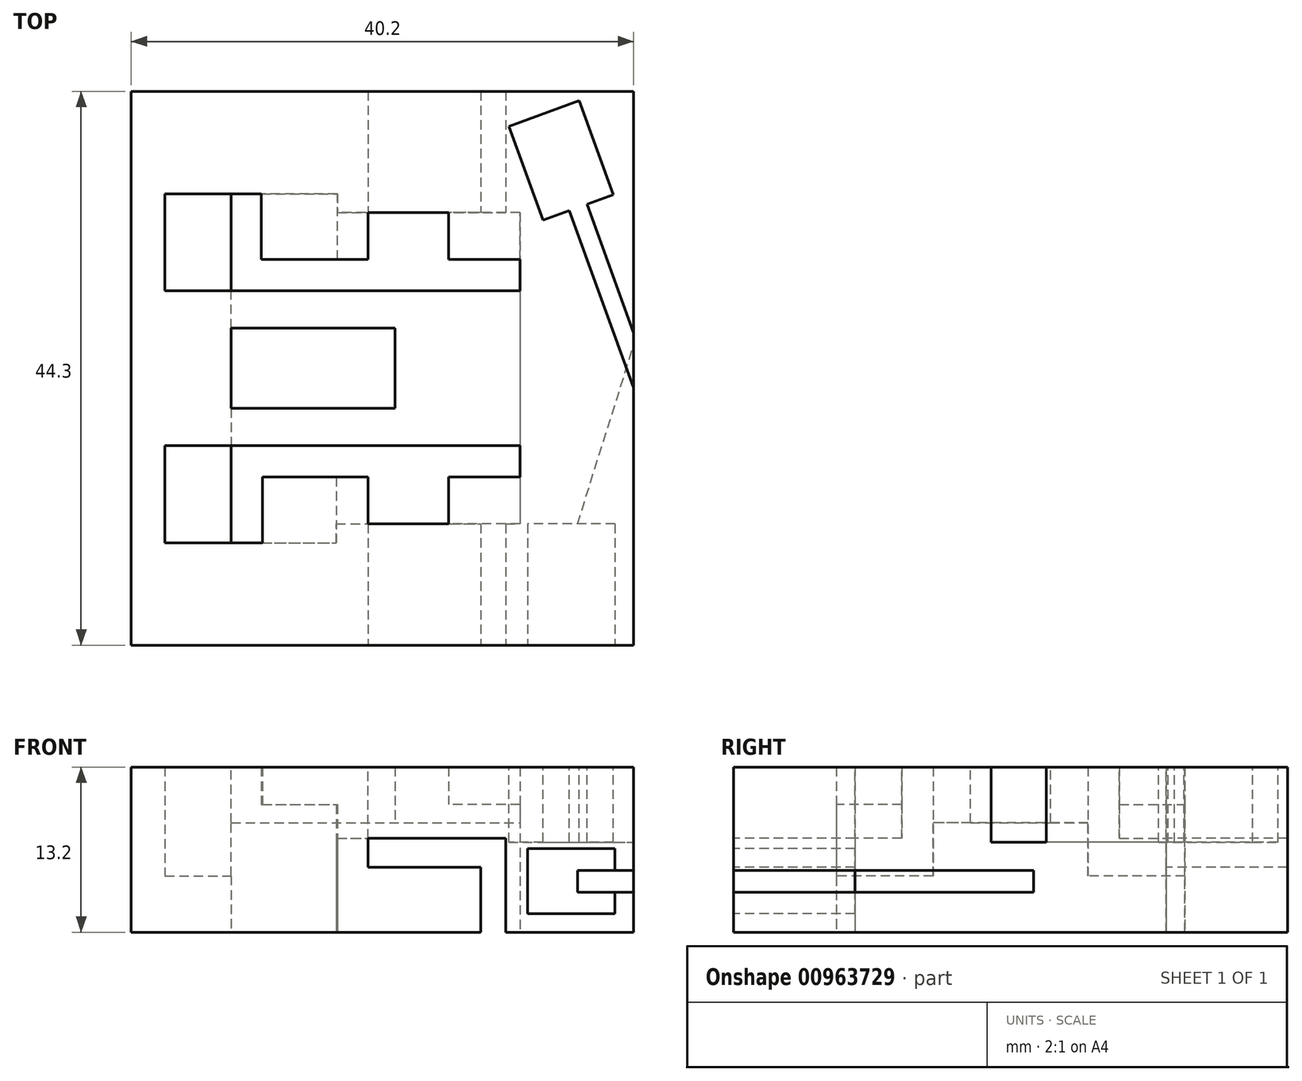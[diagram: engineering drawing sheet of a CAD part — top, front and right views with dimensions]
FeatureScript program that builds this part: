
annotation { "Feature Type Name" : "Feature", "Feature Type Description" : "" }
export const myFeature = defineFeature(function(context is Context, id is Id, definition is map)
    precondition{}
    {
        {
            var Q0;
            Q0=qCreatedBy(makeId("Front.planeOp"),FACE);
            var sketch = newSketch(context, id + "F0", { "sketchPlane" : qUnion([Q0])});
            skLineSegment(sketch, "E0.bottom", {"start": v(-40.2, 13.2) * mm, "end": v(0, 13.2) * mm});
            skLineSegment(sketch, "E0.top", {"start": v(-40.2, 0) * mm, "end": v(0, 0) * mm});
            skLineSegment(sketch, "E0.left", {"start": v(-40.2, 13.2) * mm, "end": v(-40.2, 0) * mm});
            skLineSegment(sketch, "E0.right", {"start": v(0, 13.2) * mm, "end": v(0, 0) * mm});
            skLineSegment(sketch, "E1", {"start": v(0, 3.2) * mm, "end": v(-1.5, 3.2) * mm});
            skLineSegment(sketch, "E2", {"start": v(-1.5, 3.2) * mm, "end": v(-1.5, 1.47) * mm});
            skLineSegment(sketch, "E3", {"start": v(-1.5, 1.47) * mm, "end": v(-8.5, 1.47) * mm});
            skLineSegment(sketch, "E4", {"start": v(-8.5, 1.48) * mm, "end": v(-8.5, 6.68) * mm});
            skLineSegment(sketch, "E5", {"start": v(-8.5, 6.68) * mm, "end": v(-1.5, 6.68) * mm});
            skLineSegment(sketch, "E6", {"start": v(-1.5, 6.68) * mm, "end": v(-1.5, 4.95) * mm});
            skLineSegment(sketch, "E7", {"start": v(-1.5, 4.95) * mm, "end": v(0, 4.95) * mm});
            skLineSegment(sketch, "E8", {"start": v(-10.25, 0) * mm, "end": v(-10.25, 7.5) * mm});
            skLineSegment(sketch, "E9", {"start": v(-10.25, 7.5) * mm, "end": v(-21.25, 7.5) * mm});
            skLineSegment(sketch, "E10", {"start": v(-21.25, 7.5) * mm, "end": v(-21.25, 5.2) * mm});
            skLineSegment(sketch, "E11", {"start": v(-21.25, 5.2) * mm, "end": v(-12.25, 5.2) * mm});
            skLineSegment(sketch, "E12", {"start": v(-12.25, 5.2) * mm, "end": v(-12.25, 0) * mm});
            skSolve(sketch);
        }
        {
            var Q0;
            {var subQ4=sQuery(id+"F0.wireOp",EDGE,"E0.bottom");Q0=makeQuery(id+"F0.imprint","IMPRINT",FACE,{"disambiguationData":[TD([[makeQuery(id+"F0.imprint","IMPRINT",EDGE,{"derivedFrom":subQ4}),-1.0]])]});}
            var Q1;
            {var subQ0=sQuery(id+"F0.wireOp",EDGE,"E8");Q1=makeQuery(id+"F0.imprint","IMPRINT",FACE,{"disambiguationData":[TD([[makeQuery(id+"F0.imprint","IMPRINT",EDGE,{"derivedFrom":subQ0}),1.0]])]});}
            extrude(context, id + "F1", {"entities" : qUnion([Q0, Q1]), "oppositeDirection" : true, "depth" : 9.7 * mm, "offsetDistance" : 25 * mm});
        }
        {
            var Q0;
            Q0=makeQuery(id+"F1.opExtrude","CAP_FACE",FACE,{"disambiguationData":[OSD([sQuery(id+"F0.wireOp",EDGE,"E0.bottom"),sQuery(id+"F0.wireOp",EDGE,"E0.top"),sQuery(id+"F0.wireOp",EDGE,"E0.left"),sQuery(id+"F0.wireOp",EDGE,"E0.right"),sQuery(id+"F0.wireOp",EDGE,"E1"),sQuery(id+"F0.wireOp",EDGE,"E2"),sQuery(id+"F0.wireOp",EDGE,"E3"),sQuery(id+"F0.wireOp",EDGE,"E4"),sQuery(id+"F0.wireOp",EDGE,"E5"),sQuery(id+"F0.wireOp",EDGE,"E6"),sQuery(id+"F0.wireOp",EDGE,"E7"),sQuery(id+"F0.wireOp",EDGE,"E8"),sQuery(id+"F0.wireOp",EDGE,"E9"),sQuery(id+"F0.wireOp",EDGE,"E10"),sQuery(id+"F0.wireOp",EDGE,"E11"),sQuery(id+"F0.wireOp",EDGE,"E12")])],"isStart":false});
            var sketch = newSketch(context, id + "F2", { "sketchPlane" : qUnion([Q0])});
            skLineSegment(sketch, "E13.bottom", {"start": v(9.1, 13.2) * mm, "end": v(14.8, 13.2) * mm});
            skLineSegment(sketch, "E13.top", {"start": v(9.1, 10.2) * mm, "end": v(14.8, 10.2) * mm});
            skLineSegment(sketch, "E13.left", {"start": v(9.1, 13.2) * mm, "end": v(9.1, 10.2) * mm});
            skLineSegment(sketch, "E13.right", {"start": v(14.8, 13.2) * mm, "end": v(14.8, 10.2) * mm});
            skLineSegment(sketch, "E14", {"start": v(21.25, 7.5) * mm, "end": v(21.25, 13.2) * mm});
            skLineSegment(sketch, "E15", {"start": v(21.25, 13.2) * mm, "end": v(29.7, 13.2) * mm});
            skLineSegment(sketch, "E16", {"start": v(29.7, 13.2) * mm, "end": v(29.7, 10.2) * mm});
            skLineSegment(sketch, "E17", {"start": v(29.7, 10.2) * mm, "end": v(23.8, 10.2) * mm});
            skLineSegment(sketch, "E18", {"start": v(23.8, 10.2) * mm, "end": v(23.8, 7.5) * mm});
            skLineSegment(sketch, "E19", {"start": v(23.8, 7.5) * mm, "end": v(21.25, 7.5) * mm});
            skLineSegment(sketch, "E20.bottom", {"start": v(0, 13.2) * mm, "end": v(9.1, 13.2) * mm});
            skLineSegment(sketch, "E20.top", {"start": v(0, 0) * mm, "end": v(9.1, 0) * mm});
            skLineSegment(sketch, "E20.left", {"start": v(0, 13.2) * mm, "end": v(0, 0) * mm});
            skLineSegment(sketch, "E20.right", {"start": v(9.1, 13.2) * mm, "end": v(9.1, 0) * mm});
            skLineSegment(sketch, "E21", {"start": v(37.5, 13.2) * mm, "end": v(37.5, 4.5) * mm});
            skLineSegment(sketch, "E22", {"start": v(37.5, 4.5) * mm, "end": v(32.2, 4.5) * mm});
            skLineSegment(sketch, "E23", {"start": v(32.2, 4.5) * mm, "end": v(32.2, 0) * mm});
            skSolve(sketch);
        }
        {
            var Q0;
            Q0=makeQuery(id+"F2.imprint","IMPRINT",FACE,{"disambiguationData":[TD([[makeQuery(id+"F2.imprint","IMPRINT",EDGE,{"derivedFrom":sQuery(id+"F2.wireOp",EDGE,"E14")}),-1.0]])]});
            var Q1;
            {var subQ0=sQuery(id+"F2.wireOp",EDGE,"E13.bottom");Q1=makeQuery(id+"F2.imprint","IMPRINT",FACE,{"disambiguationData":[TD([[makeQuery(id+"F2.imprint","IMPRINT",EDGE,{"derivedFrom":subQ0}),1.0]])]});}
            extrude(context, id + "F3", {"entities" : qUnion([Q0, Q1]), "operationType" : NewBodyOperationType.ADD, "depth" : 3.75 * mm, "offsetDistance" : 25 * mm});
        }
        {
            var Q0;
            {var subQ5=sQuery(id+"F2.wireOp",EDGE,"E20.bottom");Q0=makeQuery(id+"F2.imprint","IMPRINT",FACE,{"disambiguationData":[TD([[makeQuery(id+"F2.imprint","IMPRINT",EDGE,{"derivedFrom":subQ5}),1.0]])]});}
            var Q1;
            {var subQ0=makeQuery(id+"F1.opExtrude","CAP_EDGE",EDGE,{"disambiguationData":[OSD([sQuery(id+"F0.wireOp",EDGE,"E1")])],"isStart":false});Q1=makeQuery(id+"F2.imprint","IMPRINT",FACE,{"disambiguationData":[TD([[makeQuery(id+"F2.imprint","IMPRINT",EDGE,{"derivedFrom":subQ0}),1.0]])]});}
            extrude(context, id + "F4", {"entities" : qUnion([Q0, Q1]), "operationType" : NewBodyOperationType.ADD, "depth" : 24.9 * mm, "offsetDistance" : 25 * mm});
        }
        {
            var Q0;
            Q0=makeQuery(id+"F4.opExtrude","CAP_FACE",FACE,{"disambiguationData":[OSD([sQuery(id+"F2.wireOp",EDGE,"E20.bottom"),sQuery(id+"F2.wireOp",EDGE,"E20.top"),sQuery(id+"F2.wireOp",EDGE,"E20.left"),sQuery(id+"F2.wireOp",EDGE,"E20.right")])],"isStart":false});
            var sketch = newSketch(context, id + "F5", { "sketchPlane" : qUnion([Q0])});
            skLineSegment(sketch, "E24.bottom", {"start": v(0, 13.2) * mm, "end": v(40.2, 13.2) * mm});
            skLineSegment(sketch, "E24.top", {"start": v(0, 0) * mm, "end": v(40.2, 0) * mm});
            skLineSegment(sketch, "E24.left", {"start": v(0, 13.2) * mm, "end": v(0, 0) * mm});
            skLineSegment(sketch, "E24.right", {"start": v(40.2, 13.2) * mm, "end": v(40.2, 0) * mm});
            skSolve(sketch);
        }
        {
            var Q0;
            Q0 = qSketchRegion(id + "F5", true);
            extrude(context, id + "F6", {"entities" : qUnion([Q0]), "operationType" : NewBodyOperationType.ADD, "depth" : 9.7 * mm, "offsetDistance" : 25 * mm});
        }
        {
            var Q0;
            {var subQ0=sQuery(id+"F0.wireOp",EDGE,"E8");Q0=makeQuery(id+"F0.imprint","IMPRINT",FACE,{"disambiguationData":[TD([[makeQuery(id+"F0.imprint","IMPRINT",EDGE,{"derivedFrom":subQ0}),1.0]])]});}
            var Q1;
            Q1=makeQuery(id+"F6.opExtrude","CAP_FACE",FACE,{"disambiguationData":[OSD([sQuery(id+"F5.wireOp",EDGE,"E24.bottom"),sQuery(id+"F5.wireOp",EDGE,"E24.top"),sQuery(id+"F5.wireOp",EDGE,"E24.left"),sQuery(id+"F5.wireOp",EDGE,"E24.right")])],"isStart":false});
            extrude(context, id + "F7", {"entities" : qUnion([Q0]), "operationType" : NewBodyOperationType.REMOVE, "endBound" : BoundingType.UP_TO_SURFACE, "oppositeDirection" : true, "depth" : 50 * mm, "endBoundEntityFace" : qUnion([Q1]), "offsetDistance" : 25 * mm});
        }
        {
            var Q0;
            Q0=makeQuery(id+"F6.opExtrude","CAP_FACE",FACE,{"disambiguationData":[OSD([sQuery(id+"F5.wireOp",EDGE,"E24.bottom"),sQuery(id+"F5.wireOp",EDGE,"E24.top"),sQuery(id+"F5.wireOp",EDGE,"E24.left"),sQuery(id+"F5.wireOp",EDGE,"E24.right")])],"isStart":true});
            var sketch = newSketch(context, id + "F8", { "sketchPlane" : qUnion([Q0])});
            skLineSegment(sketch, "E25.bottom", {"start": v(-9.1, 13.2) * mm, "end": v(-14.8, 13.2) * mm});
            skLineSegment(sketch, "E25.top", {"start": v(-9.1, 10.2) * mm, "end": v(-14.8, 10.2) * mm});
            skLineSegment(sketch, "E25.left", {"start": v(-9.1, 13.2) * mm, "end": v(-9.1, 10.2) * mm});
            skLineSegment(sketch, "E25.right", {"start": v(-14.8, 13.2) * mm, "end": v(-14.8, 10.2) * mm});
            skLineSegment(sketch, "E26", {"start": v(-21.25, 7.5) * mm, "end": v(-21.25, 13.2) * mm});
            skLineSegment(sketch, "E27", {"start": v(-21.25, 13.2) * mm, "end": v(-29.8, 13.2) * mm});
            skLineSegment(sketch, "E28", {"start": v(-29.8, 13.2) * mm, "end": v(-29.8, 10.2) * mm});
            skLineSegment(sketch, "E29", {"start": v(-29.8, 10.2) * mm, "end": v(-23.7, 10.2) * mm});
            skLineSegment(sketch, "E30", {"start": v(-23.7, 10.2) * mm, "end": v(-23.7, 7.5) * mm});
            skLineSegment(sketch, "E31", {"start": v(-23.7, 7.5) * mm, "end": v(-21.25, 7.5) * mm});
            skSolve(sketch);
        }
        {
            var Q0;
            Q0=makeQuery(id+"F8.imprint","IMPRINT",FACE,{"disambiguationData":[TD([[makeQuery(id+"F8.imprint","IMPRINT",EDGE,{"derivedFrom":sQuery(id+"F8.wireOp",EDGE,"E25.bottom")}),1.0]])]});
            var Q1;
            Q1=makeQuery(id+"F8.imprint","IMPRINT",FACE,{"disambiguationData":[TD([[makeQuery(id+"F8.imprint","IMPRINT",EDGE,{"derivedFrom":sQuery(id+"F8.wireOp",EDGE,"E26")}),1.0]])]});
            extrude(context, id + "F9", {"entities" : qUnion([Q0, Q1]), "operationType" : NewBodyOperationType.ADD, "depth" : 3.75 * mm, "offsetDistance" : 25 * mm});
        }
        {
            var Q0;
            {var subQ3=sQuery(id+"F2.wireOp",EDGE,"E21");Q0=makeQuery(id+"F2.imprint","IMPRINT",FACE,{"disambiguationData":[TD([[makeQuery(id+"F2.imprint","IMPRINT",EDGE,{"derivedFrom":subQ3}),1.0]])]});}
            var Q1;
            {var subQ0=sQuery(id+"F5.wireOp",EDGE,"E24.right");var subQ1=sQuery(id+"F5.wireOp",EDGE,"E24.top");var subQ3=sQuery(id+"F5.wireOp",EDGE,"E24.left");var subQ4=sQuery(id+"F5.wireOp",EDGE,"E24.bottom");var subQ5=makeQuery(id+"F6.opExtrude","CAP_FACE",FACE,{"disambiguationData":[OSD([subQ4,subQ1,subQ3,subQ0])],"isStart":true});Q1=makeQuery(id+"F9.boolean.opBoolean","SPLIT",FACE,{"disambiguationData":[TD([makeQuery(id+"F6.opExtrude","SWEPT_FACE",FACE,{"disambiguationData":[OSD([subQ0])]})])],"derivedFrom":subQ5});}
            extrude(context, id + "F10", {"entities" : qUnion([Q0]), "operationType" : NewBodyOperationType.ADD, "endBound" : BoundingType.UP_TO_SURFACE, "depth" : 25 * mm, "endBoundEntityFace" : qUnion([Q1]), "offsetDistance" : 25 * mm});
        }
        {
            var Q0;
            Q0=makeQuery(id+"F4.opExtrude","SWEPT_FACE",FACE,{"disambiguationData":[OSD([sQuery(id+"F2.wireOp",EDGE,"E20.right")])]});
            var sketch = newSketch(context, id + "F11", { "sketchPlane" : qUnion([Q0])});
            skPoint(sketch, "E32.firstSnap0", {"position": v(-31.27, 13.2) * mm});
            skLineSegment(sketch, "E32.bottom", {"start": v(-28.35, 13.2) * mm, "end": v(-25.35, 13.2) * mm});
            skLineSegment(sketch, "E32.top", {"start": v(-28.35, 8.75) * mm, "end": v(-25.35, 8.75) * mm});
            skLineSegment(sketch, "E32.left", {"start": v(-28.35, 13.2) * mm, "end": v(-28.35, 8.75) * mm});
            skLineSegment(sketch, "E32.right", {"start": v(-25.35, 13.2) * mm, "end": v(-25.35, 8.75) * mm});
            skLineSegment(sketch, "E33.bottom", {"start": v(-18.95, 13.2) * mm, "end": v(-15.95, 13.2) * mm});
            skLineSegment(sketch, "E33.top", {"start": v(-18.95, 8.75) * mm, "end": v(-15.95, 8.75) * mm});
            skLineSegment(sketch, "E33.left", {"start": v(-18.95, 13.2) * mm, "end": v(-18.95, 8.75) * mm});
            skLineSegment(sketch, "E33.right", {"start": v(-15.95, 13.2) * mm, "end": v(-15.95, 8.75) * mm});
            skLineSegment(sketch, "E34", {"start": v(-25.35, 13.2) * mm, "end": v(-18.95, 13.2) * mm, "construction": true});
            skLineSegment(sketch, "E35", {"start": v(-25.35, 8.75) * mm, "end": v(-18.95, 8.75) * mm, "construction": true});
            skSolve(sketch);
        }
        {
            var Q0;
            Q0=makeQuery(id+"F11.imprint","IMPRINT",FACE,{"disambiguationData":[TD([[makeQuery(id+"F11.imprint","IMPRINT",EDGE,{"derivedFrom":sQuery(id+"F11.wireOp",EDGE,"E32.bottom")}),-1.0]])]});
            var Q1;
            Q1=makeQuery(id+"F11.imprint","IMPRINT",FACE,{"disambiguationData":[TD([[makeQuery(id+"F11.imprint","IMPRINT",EDGE,{"derivedFrom":sQuery(id+"F11.wireOp",EDGE,"E33.bottom")}),-1.0]])]});
            var Q2;
            Q2=makeQuery(id+"F10.opExtrude","SWEPT_FACE",FACE,{"disambiguationData":[OSD([sQuery(id+"F2.wireOp",EDGE,"E21")])]});
            extrude(context, id + "F12", {"entities" : qUnion([Q0, Q1]), "operationType" : NewBodyOperationType.ADD, "endBound" : BoundingType.UP_TO_SURFACE, "depth" : 25 * mm, "endBoundEntityFace" : qUnion([Q2]), "offsetDistance" : 25 * mm});
        }
        {
            var Q0;
            Q0=makeQuery(id+"F12.opExtrude","SWEPT_FACE",FACE,{"disambiguationData":[OSD([sQuery(id+"F11.wireOp",EDGE,"E32.right")])]});
            var sketch = newSketch(context, id + "F13", { "sketchPlane" : qUnion([Q0])});
            skLineSegment(sketch, "E36", {"start": v(-19.1, 13.2) * mm, "end": v(-19.1, 8.75) * mm});
            skLineSegment(sketch, "E37", {"start": v(-19.1, 8.75) * mm, "end": v(-18.1, 8.75) * mm});
            skSolve(sketch);
        }
        {
            var Q0;
            {var subQ3=sQuery(id+"F13.wireOp",EDGE,"E36");Q0=makeQuery(id+"F13.imprint","IMPRINT",FACE,{"disambiguationData":[TD([[makeQuery(id+"F13.imprint","IMPRINT",EDGE,{"derivedFrom":subQ3}),1.0]])]});}
            var Q1;
            Q1=makeQuery(id+"F12.opExtrude","SWEPT_FACE",FACE,{"disambiguationData":[OSD([sQuery(id+"F11.wireOp",EDGE,"E33.left")])]});
            extrude(context, id + "F14", {"entities" : qUnion([Q0]), "operationType" : NewBodyOperationType.ADD, "endBound" : BoundingType.UP_TO_SURFACE, "depth" : 25 * mm, "endBoundEntityFace" : qUnion([Q1]), "offsetDistance" : 25 * mm});
        }
        {
            var Q0;
            Q0=makeQuery(id+"F10.opExtrude","SWEPT_FACE",FACE,{"disambiguationData":[OSD([sQuery(id+"F2.wireOp",EDGE,"E21")])]});
            var sketch = newSketch(context, id + "F15", { "sketchPlane" : qUnion([Q0])});
            skLineSegment(sketch, "E38", {"start": v(18.95, 8.75) * mm, "end": v(18.95, 4.5) * mm});
            skLineSegment(sketch, "E39", {"start": v(25.35, 8.75) * mm, "end": v(25.35, 4.5) * mm});
            skSolve(sketch);
        }
        {
            var Q0;
            {var subQ5=sQuery(id+"F15.wireOp",EDGE,"E38");Q0=makeQuery(id+"F15.imprint","IMPRINT",FACE,{"disambiguationData":[TD([[makeQuery(id+"F15.imprint","IMPRINT",EDGE,{"derivedFrom":subQ5}),1.0]])]});}
            var Q1;
            Q1=makeQuery(id+"F10.opExtrude","SWEPT_FACE",FACE,{"disambiguationData":[OSD([sQuery(id+"F2.wireOp",EDGE,"E23")])]});
            extrude(context, id + "F16", {"entities" : qUnion([Q0]), "operationType" : NewBodyOperationType.ADD, "endBound" : BoundingType.UP_TO_SURFACE, "depth" : 25 * mm, "endBoundEntityFace" : qUnion([Q1]), "offsetDistance" : 25 * mm});
        }
        {
            var Q0;
            {var subQ0=sQuery(id+"F11.wireOp",EDGE,"E32.top");Q0=makeQuery(id+"F14.boolean.opBoolean","MERGE",FACE,{"derivedFrom":[makeQuery(id+"F12.opExtrude","SWEPT_FACE",FACE,{"disambiguationData":[OSD([subQ0])]}),makeQuery(id+"F12.opExtrude","SWEPT_FACE",FACE,{"disambiguationData":[OSD([sQuery(id+"F11.wireOp",EDGE,"E33.top")])]}),makeQuery(id+"F14.opExtrude","SWEPT_FACE",FACE,{"disambiguationData":[OSD([subQ0,sQuery(id+"F11.wireOp",EDGE,"E32.right"),sQuery(id+"F13.wireOp",EDGE,"E37")])]})]});}
            var sketch = newSketch(context, id + "F17", { "sketchPlane" : qUnion([Q0])});
            skLineSegment(sketch, "E40", {"start": v(-32.2, -25.35) * mm, "end": v(-32.2, -28.35) * mm});
            skLineSegment(sketch, "E41", {"start": v(-32.2, -18.95) * mm, "end": v(-32.2, -15.95) * mm});
            skSolve(sketch);
        }
        {
            var Q0;
            {var subQ0=sQuery(id+"F17.wireOp",EDGE,"E41");Q0=makeQuery(id+"F17.imprint","IMPRINT",FACE,{"disambiguationData":[TD([[makeQuery(id+"F17.imprint","IMPRINT",EDGE,{"derivedFrom":subQ0}),1.0]])]});}
            var Q1;
            {var subQ0=sQuery(id+"F17.wireOp",EDGE,"E40");Q1=makeQuery(id+"F17.imprint","IMPRINT",FACE,{"disambiguationData":[TD([[makeQuery(id+"F17.imprint","IMPRINT",EDGE,{"derivedFrom":subQ0}),-1.0]])]});}
            var Q2;
            {var subQ1=sQuery(id+"F15.wireOp",EDGE,"E39");var subQ2=sQuery(id+"F11.wireOp",EDGE,"E32.right");var subQ3=sQuery(id+"F2.wireOp",EDGE,"E22");Q2=makeQuery(id+"F16.boolean.opBoolean","SPLIT",FACE,{"disambiguationData":[TD([makeQuery(id+"F16.opExtrude","SWEPT_FACE",FACE,{"disambiguationData":[OSD([subQ2,subQ1])]})])],"derivedFrom":makeQuery(id+"F10.opExtrude","SWEPT_FACE",FACE,{"disambiguationData":[OSD([subQ3])]})});}
            extrude(context, id + "F18", {"entities" : qUnion([Q0, Q1]), "operationType" : NewBodyOperationType.ADD, "endBound" : BoundingType.UP_TO_SURFACE, "depth" : 25 * mm, "endBoundEntityFace" : qUnion([Q2]), "offsetDistance" : 25 * mm});
        }
        {
            var Q0;
            {var subQ0=sQuery(id+"F2.wireOp",EDGE,"E23");var subQ1=sQuery(id+"F2.wireOp",EDGE,"E22");Q0=makeQuery(id+"F18.boolean.opBoolean","MERGE",FACE,{"derivedFrom":[makeQuery(id+"F16.boolean.opBoolean","MERGE",FACE,{"derivedFrom":[makeQuery(id+"F10.opExtrude","SWEPT_FACE",FACE,{"disambiguationData":[OSD([subQ0])]}),makeQuery(id+"F16.opExtrude","CAP_FACE",FACE,{"disambiguationData":[OSD([sQuery(id+"F0.wireOp",EDGE,"E0.bottom"),sQuery(id+"F2.wireOp",EDGE,"E21"),subQ1,sQuery(id+"F11.wireOp",EDGE,"E32.right"),sQuery(id+"F11.wireOp",EDGE,"E33.left"),sQuery(id+"F15.wireOp",EDGE,"E38"),sQuery(id+"F15.wireOp",EDGE,"E39")])],"isStart":false})]}),makeQuery(id+"F18.opExtrude","SWEPT_FACE",FACE,{"disambiguationData":[OSD([subQ1,subQ0])]}),makeQuery(id+"F18.opExtrude","SWEPT_FACE",FACE,{"disambiguationData":[OSD([sQuery(id+"F17.wireOp",EDGE,"E40")])]}),makeQuery(id+"F18.opExtrude","SWEPT_FACE",FACE,{"disambiguationData":[OSD([sQuery(id+"F17.wireOp",EDGE,"E41")])]})]});}
            var sketch = newSketch(context, id + "F19", { "sketchPlane" : qUnion([Q0])});
            skLineSegment(sketch, "E42.bottom", {"start": v(20.65, 13.2) * mm, "end": v(23.65, 13.2) * mm});
            skLineSegment(sketch, "E42.top", {"start": v(20.65, 10.2) * mm, "end": v(23.65, 10.2) * mm});
            skLineSegment(sketch, "E42.left", {"start": v(20.65, 13.2) * mm, "end": v(20.65, 10.2) * mm});
            skLineSegment(sketch, "E42.right", {"start": v(23.65, 13.2) * mm, "end": v(23.65, 10.2) * mm});
            skLineSegment(sketch, "E43", {"start": v(20.65, 13.2) * mm, "end": v(18.95, 13.2) * mm, "construction": true});
            skLineSegment(sketch, "E44", {"start": v(23.65, 13.2) * mm, "end": v(25.35, 13.2) * mm, "construction": true});
            skSolve(sketch);
        }
        {
            var Q0;
            Q0=makeQuery(id+"F1.opExtrude","SWEPT_FACE",FACE,{"disambiguationData":[OSD([sQuery(id+"F0.wireOp",EDGE,"E7")])]});
            var sketch = newSketch(context, id + "F20", { "sketchPlane" : qUnion([Q0])});
            skLineSegment(sketch, "E45", {"start": v(0, -9.7) * mm, "end": v(0, -24) * mm});
            skLineSegment(sketch, "E46", {"start": v(0, -24) * mm, "end": v(-4.5, -9.7) * mm});
            skLineSegment(sketch, "E47", {"start": v(-4.5, -9.7) * mm, "end": v(0, -9.7) * mm});
            skSolve(sketch);
        }
        {
            var Q0;
            Q0 = qSketchRegion(id + "F20", true);
            var Q1;
            Q1=makeQuery(id+"F1.opExtrude","SWEPT_FACE",FACE,{"disambiguationData":[OSD([sQuery(id+"F0.wireOp",EDGE,"E1")])]});
            extrude(context, id + "F21", {"entities" : qUnion([Q0]), "operationType" : NewBodyOperationType.REMOVE, "endBound" : BoundingType.UP_TO_SURFACE, "depth" : 25 * mm, "endBoundEntityFace" : qUnion([Q1]), "offsetDistance" : 25 * mm});
        }
        {
            var Q0;
            {var subQ0=sQuery(id+"F0.wireOp",EDGE,"E0.bottom");var subQ1=sQuery(id+"F11.wireOp",EDGE,"E32.bottom");var subQ2=sQuery(id+"F2.wireOp",EDGE,"E20.bottom");var subQ3=sQuery(id+"F2.wireOp",EDGE,"E13.bottom");Q0=makeQuery(id+"FeJcqMP7s32EqgO_1.boolean.opBoolean","MERGE",FACE,{"derivedFrom":[makeQuery(id+"F16.boolean.opBoolean","MERGE",FACE,{"derivedFrom":[makeQuery(id+"F14.boolean.opBoolean","MERGE",FACE,{"derivedFrom":[makeQuery(id+"F12.boolean.opBoolean","MERGE",FACE,{"derivedFrom":[makeQuery(id+"F10.boolean.opBoolean","MERGE",FACE,{"derivedFrom":[makeQuery(id+"F9.boolean.opBoolean","MERGE",FACE,{"derivedFrom":[makeQuery(id+"F6.boolean.opBoolean","MERGE",FACE,{"derivedFrom":[makeQuery(id+"F4.boolean.opBoolean","MERGE",FACE,{"derivedFrom":[makeQuery(id+"F3.boolean.opBoolean","MERGE",FACE,{"derivedFrom":[makeQuery(id+"F1.opExtrude","SWEPT_FACE",FACE,{"disambiguationData":[OSD([subQ0])]}),makeQuery(id+"F3.opExtrude","SWEPT_FACE",FACE,{"disambiguationData":[OSD([subQ3])]}),makeQuery(id+"F3.opExtrude","SWEPT_FACE",FACE,{"disambiguationData":[OSD([sQuery(id+"F2.wireOp",EDGE,"E15")])]})]}),makeQuery(id+"F4.opExtrude","SWEPT_FACE",FACE,{"disambiguationData":[OSD([subQ2])]})]}),makeQuery(id+"F6.opExtrude","SWEPT_FACE",FACE,{"disambiguationData":[OSD([sQuery(id+"F5.wireOp",EDGE,"E24.bottom")])]})]}),makeQuery(id+"F9.opExtrude","SWEPT_FACE",FACE,{"disambiguationData":[OSD([sQuery(id+"F8.wireOp",EDGE,"E25.bottom")])]}),makeQuery(id+"F9.opExtrude","SWEPT_FACE",FACE,{"disambiguationData":[OSD([sQuery(id+"F8.wireOp",EDGE,"E27")])]})]}),makeQuery(id+"F10.opExtrude","SWEPT_FACE",FACE,{"disambiguationData":[OSD([subQ0])]})]}),makeQuery(id+"F12.opExtrude","SWEPT_FACE",FACE,{"disambiguationData":[OSD([subQ1])]}),makeQuery(id+"F12.opExtrude","SWEPT_FACE",FACE,{"disambiguationData":[OSD([sQuery(id+"F11.wireOp",EDGE,"E33.bottom")])]})]}),makeQuery(id+"F14.opExtrude","SWEPT_FACE",FACE,{"disambiguationData":[OSD([subQ3,subQ2,sQuery(id+"F2.wireOp",EDGE,"E20.right"),subQ1,sQuery(id+"F11.wireOp",EDGE,"E32.right")])]})]}),makeQuery(id+"F16.opExtrude","SWEPT_FACE",FACE,{"disambiguationData":[OSD([subQ0,sQuery(id+"F2.wireOp",EDGE,"E21")])]})]}),makeQuery(id+"FeJcqMP7s32EqgO_1.opExtrude","SWEPT_FACE",FACE,{"disambiguationData":[OSD([sQuery(id+"F19.wireOp",EDGE,"E42.bottom")])]})]});}
            var sketch = newSketch(context, id + "F22", { "sketchPlane" : qUnion([Q0])});
            skLineSegment(sketch, "E48", {"start": v(-10, 41.5) * mm, "end": v(-4.36, 43.55) * mm});
            skLineSegment(sketch, "E49", {"start": v(-4.36, 43.55) * mm, "end": v(-1.63, 36.03) * mm});
            skLineSegment(sketch, "E50", {"start": v(-1.63, 36.03) * mm, "end": v(-3.74, 35.27) * mm});
            skLineSegment(sketch, "E51", {"start": v(-7.26, 33.98) * mm, "end": v(-10, 41.5) * mm});
            skLineSegment(sketch, "E52", {"start": v(-3.74, 35.27) * mm, "end": v(0, 24.99) * mm});
            skLineSegment(sketch, "E53", {"start": v(-5.15, 34.75) * mm, "end": v(0, 20.6) * mm});
            skLineSegment(sketch, "E54", {"start": v(-7.26, 33.98) * mm, "end": v(-5.15, 34.75) * mm});
            skLineSegment(sketch, "E55", {"start": v(-3.74, 35.27) * mm, "end": v(-1.63, 36.03) * mm});
            skLineSegment(sketch, "E56.trimOffspring", {"start": v(-5.15, 34.75) * mm, "end": v(-7.26, 33.98) * mm});
            skSolve(sketch);
        }
        {
            var Q0;
            Q0=makeQuery(id+"F22.imprint","IMPRINT",FACE,{"disambiguationData":[TD([[makeQuery(id+"F22.imprint","IMPRINT",EDGE,{"derivedFrom":sQuery(id+"F22.wireOp",EDGE,"E48")}),-1.0]])]});
            extrude(context, id + "F23", {"entities" : qUnion([Q0]), "operationType" : NewBodyOperationType.REMOVE, "oppositeDirection" : true, "depth" : 6 * mm, "offsetDistance" : 25 * mm});
        }
        {
            var Q0;
            {var subQ2=sQuery(id+"F5.wireOp",EDGE,"E24.right");Q0=makeQuery(id+"F5.imprint","IMPRINT",FACE,{"disambiguationData":[TD([[makeQuery(id+"F5.imprint","IMPRINT",EDGE,{"derivedFrom":subQ2}),-1.0]])]});}
            var sketch = newSketch(context, id + "F24", { "sketchPlane" : qUnion([Q0])});
            skLineSegment(sketch, "E57", {"start": v(23.7, 7.5) * mm, "end": v(23.7, 0) * mm});
            skLineSegment(sketch, "E58", {"start": v(32.2, 0) * mm, "end": v(23.7, 0) * mm});
            skLineSegment(sketch, "E59", {"start": v(32.2, 0) * mm, "end": v(32.2, 4.5) * mm});
            skLineSegment(sketch, "E60", {"start": v(32.2, 4.5) * mm, "end": v(37.5, 4.5) * mm});
            skLineSegment(sketch, "E61", {"start": v(37.5, 4.5) * mm, "end": v(37.5, 13.2) * mm});
            skLineSegment(sketch, "E62", {"start": v(37.5, 13.2) * mm, "end": v(29.8, 13.2) * mm});
            skLineSegment(sketch, "E63", {"start": v(29.8, 13.2) * mm, "end": v(29.8, 10.2) * mm});
            skLineSegment(sketch, "E64", {"start": v(29.8, 10.2) * mm, "end": v(23.7, 10.2) * mm});
            skLineSegment(sketch, "E65", {"start": v(23.7, 10.2) * mm, "end": v(23.7, 7.5) * mm});
            skSolve(sketch);
        }
        {
            var Q0;
            Q0=makeQuery(id+"F24.imprint","IMPRINT",FACE,{"disambiguationData":[TD([[makeQuery(id+"F24.imprint","IMPRINT",EDGE,{"derivedFrom":sQuery(id+"F24.wireOp",EDGE,"E57")}),1.0]])]});
            extrude(context, id + "F25", {"entities" : qUnion([Q0]), "operationType" : NewBodyOperationType.REMOVE, "depth" : 1.5 * mm, "offsetDistance" : 25 * mm});
        }
        {
            var Q0;
            {var subQ1=sQuery(id+"F2.wireOp",EDGE,"E13.top");Q0=makeQuery(id+"F2.imprint","IMPRINT",FACE,{"disambiguationData":[TD([[makeQuery(id+"F2.imprint","IMPRINT",EDGE,{"derivedFrom":subQ1}),-1.0]])]});}
            var sketch = newSketch(context, id + "F26", { "sketchPlane" : qUnion([Q0])});
            skLineSegment(sketch, "E66", {"start": v(23.8, 10.2) * mm, "end": v(23.8, 0) * mm});
            skLineSegment(sketch, "E67", {"start": v(23.8, 0) * mm, "end": v(32.2, 0) * mm});
            skLineSegment(sketch, "E68", {"start": v(32.2, 0) * mm, "end": v(32.2, 4.5) * mm});
            skLineSegment(sketch, "E69", {"start": v(32.2, 4.5) * mm, "end": v(37.5, 4.5) * mm});
            skLineSegment(sketch, "E70", {"start": v(37.5, 4.5) * mm, "end": v(37.5, 13.2) * mm});
            skLineSegment(sketch, "E71", {"start": v(37.5, 13.2) * mm, "end": v(29.7, 13.2) * mm});
            skLineSegment(sketch, "E72", {"start": v(29.7, 13.2) * mm, "end": v(29.7, 10.2) * mm});
            skLineSegment(sketch, "E73", {"start": v(29.7, 10.2) * mm, "end": v(23.8, 10.2) * mm});
            skSolve(sketch);
        }
        {
            var Q0;
            {var subQ0=sQuery(id+"F26.wireOp",EDGE,"E67");Q0=makeQuery(id+"F26.imprint","IMPRINT",FACE,{"disambiguationData":[TD([[makeQuery(id+"F26.imprint","IMPRINT",EDGE,{"derivedFrom":subQ0}),-1.0]])]});}
            extrude(context, id + "F27", {"entities" : qUnion([Q0]), "operationType" : NewBodyOperationType.REMOVE, "oppositeDirection" : true, "depth" : 1.5 * mm, "offsetDistance" : 25 * mm});
        }
    });
